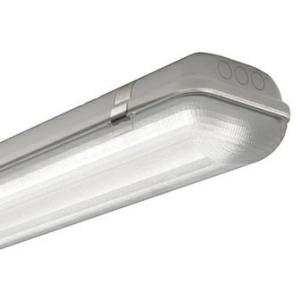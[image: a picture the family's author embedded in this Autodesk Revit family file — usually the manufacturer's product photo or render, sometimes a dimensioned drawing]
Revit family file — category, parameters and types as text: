
# Revit family: 3f_filippi_-_3f_linda_hq_3f_filippi_-_58872_-_3f_linda_led_2x30w-940_l1570
name_source: partatom
category: Lighting Fixtures
units: mm (PartAtom-declared; Revit-internal decimal feet)

## family parameters
Cut with Voids When Loaded = No
Host = Face
Light Source = No
Part Type = Normal
Room Calculation Point = No
Round Connector Dimension = Use Diameter
Shared = No

## types (1)
- 3F Filippi - 3F Linda HQ (1 x LED, 7529 lm, 66 W, 4000 K)
    Apparent Load = 66 VA
    Approval mark = CE
    CIE Flux Codes = 46 76 93 97 100
    Color Rendering = 90
    Color Temperature = 4000 K
    Control Gear = Electronic ballast
    Default Elevation = 1800 mm
    Description = ILLUMINOTECHNICAL
Luminous efficiency 100% (DLOR 97%, ULOR 3%).
Initial luminous flux of the luminaire 7529 lm.
Controlled symmetric distribution.
Installation Interdistance Transv.D = 1.52 x hu - Long.D = 1.17 x hu.
Tabular UGR (CIE 117 - 4H-8H; S=0.25H; 70/50/20): RUG 23.5 - 22.7.
Beam angle: 94° - 78°.
Luminous efficacy 114 lm/W.
Lifetime (L93/B10): 30000 h. (tq+25°C)
Lifetime (L90/B10): 50000 h. (tq+25°C)
Lifetime (L85/B10): 80000 h. (tq+25°C)
Lifetime (L80/B10): 100000 h. (tq+25°C)
Lifetime (L85/B10): 50000 h. (tq+35°C)
Sudden decreased luminous flux after 50000 hours: 0% (C0).
Photobiological safety in compliance with IEC/TR 62778: RG0 risk exempt, (IEC 62471).
In compliance with IEC/EN 62722-2-1 - IEC/EN 62717 standards.

SOURCE
2 linear LED modules 30W/940.
Energy efficiency class (UE 2019/2020 - UE 2019/2015): E.
CIE 13.3 Colour rendering index: CRI >90 (R9 >50%).
IES TM-30 Fidelity Index: Rf = 92 Rg = 101.
CCT nominal colour temperature 4000 K.
Colour initial tolerance (MacAdam): SDCM 3.

MECHANICAL
Self-extinguishing V2 polycarbonate housing, injection moulded, RAL 7035 grey.
Ecologic anti-aging injected sealing gasket.
Diffuser in self-extinguishing V2 polycarbonate, photo-engraved interior, UV stabilised, injection moulded with smooth outer surface, tamper-proof opening.
Gear-holder reflector in hot-dip galvanised steel, painted with white polyester base.
Snug fit safety snap-lock clips for diffuser mounting in stainless steel, screwdriver opening.
Fixing brackets in stainless steel.
Possibility for technicians to access the interior of the luminaire.
Luminaire with limited surface temperature. - D - (EN 60598-2-24)
Dimensions: 1570x160 mm, height 100 mm. Weight 3.348 kg.
IP66 protection degree.
Mechanical strength to impacts IK10 (20 joule).
Glow-wire test resistance 850°C.

ELECTRICAL
Halogen Free electronic wiring 230V-50/60Hz, power factor 0.97, THD <25%, constant output current, SELV, class I, 1 driver.
Power of the luminaire 66 W.
ENEC - CE.
SAFE FLICKER: PstLM=<1 and SVM=<0.4 (IEC TR 61547-1 and IEC TR 63158), to ensure a more comfortable and safe light.
Luminaire compliant with EN 60598-2-22 for power supply from a centralised emergency system CPSS (Central Power Supply System), not incorporated in the luminaire - high risk areas excluded. The default power and flux are 100% in AC and 100% in DC.
Ambient temperature from -20°C to +35°C.
Temperature class T6 max 85°C.
Relative humidity UR: <85%.

INSTALLATION
Ceiling / Suspended / Wall.
All accessories dedicated to this product are available on the Catalog and on our website www.3F-Filippi.com.

APPLICATIONS
Suitable product for food production plants (HACCP), IFS (Food Version 6), BRC (GSFS Food Version 7).
Dry, dusty indoor environments, subject to occasional water splashes.
Virtually shatterproof polycarbonate compatibly with the fumes / atmospheres that compromise the elasticity of plastic materials.
Not suitable for installation on surfaces subject to important vibrations, exposed to weather conditions, on ropes or poles.
Suitable for illumination of public car parks and parking grounds referred to DIN 67528:2018-04.

WARNING
Fixture not suitable for cold stores with an ambient temperature <0°C and/or relative humidity >85%.
Luminaire designed for disposal/recycling at end-of-life.
Replaceable (LED only) light source by a professional. Replaceable control gear by a professional.
    Height = 100 mm  [stored 0.328084 ft]
    Lamp = 1 x LED
    Lamp Light Flux = 7529 lm
    Lamp Power = 66 W
    Lamp count = 1
    Length = 1570 mm
    Lifetime = 50000 h
    Luminous efficacy = 114 lm/W
    Manufacturer = 3F Filippi
    ModVariant = No
    Model = 3F Filippi - 58872 - 3F Linda LED 2x30W-940 L1570
    Mounting Place = Ceiling
    Mounting Type = Pendant
    Number of Poles = 1
    OnlyDefault = Yes
    Power Factor = 1
    Product Name = 3F Filippi - 3F Linda HQ
    Product group = pendant luminaire
    ProductGroupID = 9
    Protection Class = Protection class I
    Protection Degree = IP 66
    RLX_Detail_Level = 1
    RLX_Emergency_Light_Flux = 0 lm
    RLX_Emergency_Type = 0
    RLX_Emergency_Type_DB = No
    RlxData = <blob elided: 71397 chars, md5=1437c6b8>
    Socket = socket
    Standby Power = 0 W
    System Light Flux = 7529 lm
    System Power = 66 W
    Type Comments = Product without accessories
    Type Image = 3ffilippi_3f_linda_led_2x.jpg
    URL = http://relux.com
    VarID = ---
    Voltage = 0 V
    Weight = 0.00 kg
    Width = 160 mm

note: [stored X ft] marks values corroborated as IEEE doubles in the binary element streams (Revit-internal decimal feet)

## geometry (parser evidence)
native form markers: Blend x4, Sweep x8
no freeform markers — native parametric forms only
